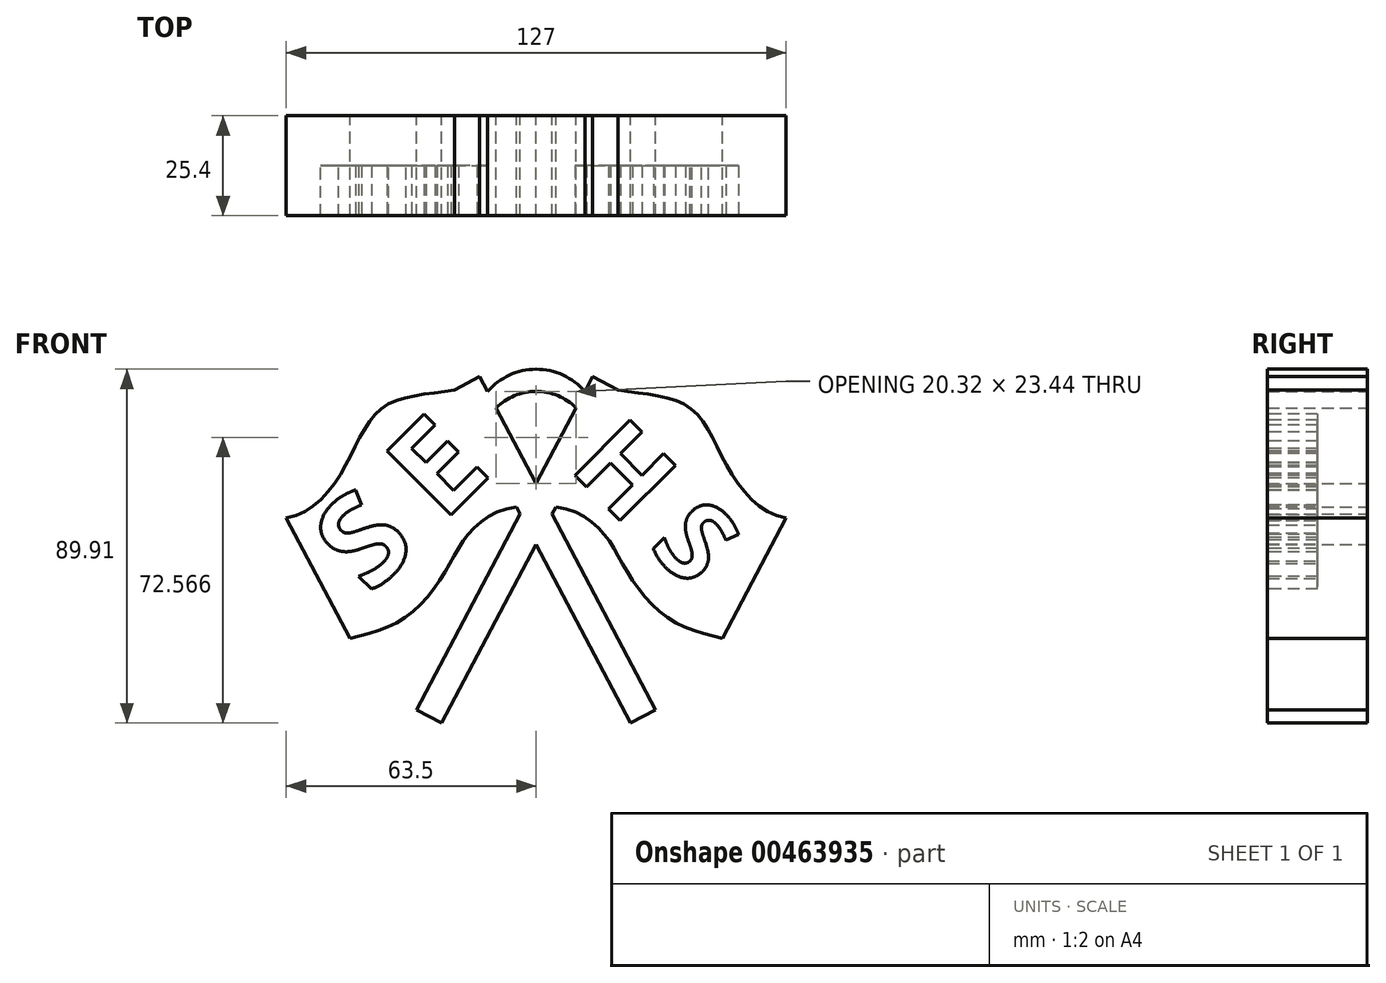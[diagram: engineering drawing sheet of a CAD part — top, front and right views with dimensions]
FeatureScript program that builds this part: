
annotation { "Feature Type Name" : "Feature", "Feature Type Description" : "" }
export const myFeature = defineFeature(function(context is Context, id is Id, definition is map)
    precondition{}
    {
        {
            var Q0;
            Q0=qCreatedBy(makeId("Front.planeOp"),FACE);
            var sketch = newSketch(context, id + "F0", { "sketchPlane" : qUnion([Q0])});
            skFitSpline(sketch, "E0", {"points": [v(20.74, 46.13) * mm, v(38.68, 41.85) * mm, v(48.5, 26.84) * mm, v(63.5, 13.57) * mm], "startDerivative": vector(58.41, -10.52) * mm, "endDerivative": vector(58.76, -8.59) * mm});
            skFitSpline(sketch, "E1.MirrorCS", {"points": [v(-20.74, 46.13) * mm, v(-38.68, 41.85) * mm, v(-48.5, 26.84) * mm, v(-63.5, 13.57) * mm], "startDerivative": vector(-58.41, -10.52) * mm, "endDerivative": vector(-58.76, -8.59) * mm});
            skLineSegment(sketch, "E2", {"start": v(-20.74, 46.13) * mm, "end": v(23.99, -38.53) * mm});
            skLineSegment(sketch, "E3.MirrorCS", {"start": v(20.74, 46.13) * mm, "end": v(-23.99, -38.53) * mm});
            skLineSegment(sketch, "E4", {"start": v(-63.5, 13.57) * mm, "end": v(-47.34, -17.03) * mm});
            skLineSegment(sketch, "E5.MirrorCS", {"start": v(63.5, 13.57) * mm, "end": v(47.34, -17.03) * mm});
            skFitSpline(sketch, "E6", {"points": [v(-47.34, -17.03) * mm, v(-33.48, -11.83) * mm, v(-23.1, 0) * mm, v(-16.74, 10.1) * mm, v(-5, 16.35) * mm], "startDerivative": vector(56.45, 14.98) * mm, "endDerivative": vector(61.73, 6.36) * mm});
            skFitSpline(sketch, "E7.MirrorCS", {"points": [v(47.34, -17.03) * mm, v(33.48, -11.83) * mm, v(23.1, 0) * mm, v(16.74, 10.1) * mm, v(5, 16.35) * mm], "startDerivative": vector(-56.45, 14.98) * mm, "endDerivative": vector(-61.73, 6.36) * mm});
            skLineSegment(sketch, "E8", {"start": v(-20.74, 46.13) * mm, "end": v(-14.36, 49.5) * mm});
            skLineSegment(sketch, "E9", {"start": v(-14.36, 49.5) * mm, "end": v(30.36, -35.16) * mm});
            skLineSegment(sketch, "E10", {"start": v(30.36, -35.16) * mm, "end": v(23.99, -38.53) * mm});
            skLineSegment(sketch, "E11.MirrorCS", {"start": v(14.36, 49.5) * mm, "end": v(-30.36, -35.16) * mm});
            skLineSegment(sketch, "E12.MirrorCS", {"start": v(20.74, 46.13) * mm, "end": v(14.36, 49.5) * mm});
            skLineSegment(sketch, "E13.MirrorCS", {"start": v(-30.36, -35.16) * mm, "end": v(-23.99, -38.53) * mm});
            skSolve(sketch);
        }
        {
            var Q0;
            Q0 = qSketchRegion(id + "F0", true);
            extrude(context, id + "F1", {"entities" : qUnion([Q0]), "depth" : 25.4 * mm});
        }
        {
            var Q0;
            Q0=qCreatedBy(makeId("Front.planeOp"),FACE);
            var sketch = newSketch(context, id + "F2", { "sketchPlane" : qUnion([Q0])});
            skArc(sketch, "E14", {"start": v(14.4, 42.7) * mm, "mid": v(-0.45, 51.38) * mm, "end": v(-14.8, 41.88) * mm});
            skArc(sketch, "E15", {"start": v(12.4, 38.62) * mm, "mid": v(-0.34, 45.75) * mm, "end": v(-12.74, 38.03) * mm});
            skLineSegment(sketch, "E16", {"start": v(-14.8, 41.88) * mm, "end": v(-12.74, 38.03) * mm});
            skLineSegment(sketch, "E17", {"start": v(14.4, 42.7) * mm, "end": v(12.4, 38.62) * mm});
            skSolve(sketch);
        }
        {
            var Q0;
            Q0 = qSketchRegion(id + "F2", true);
            extrude(context, id + "F3", {"entities" : qUnion([Q0]), "operationType" : NewBodyOperationType.ADD, "depth" : 25.4 * mm});
        }
        {
            var Q0;
            Q0=qCreatedBy(makeId("Front.planeOp"),FACE);
            cPlane(context, id + "F4", {"entities" : qUnion([Q0]), "cplaneType" : CPlaneType.OFFSET, "offset" : 25.4 * mm, "width" : 152.4 * mm, "height" : 152.4 * mm});
        }
        {
            var Q0;
            Q0=qCreatedBy(id+"F4.planeOp",FACE);
            var sketch = newSketch(context, id + "F5", { "sketchPlane" : qUnion([Q0])});
            skText(sketch, "E18", { "text": "S E", "fontName": "OpenSans-Bold.ttf"});
            skText(sketch, "E19", { "text": "H S", "fontName": "OpenSans-Bold.ttf"});
            const initialGuessF5  = {"E18": [-0.04214, -0.00623, 0.7071, 0.7071, 0.02325], "E19": [0.00811, 0.02621, 0.7071, -0.7071, 0.01999]};
            skSetInitialGuess(sketch, initialGuessF5);
            skSolve(sketch);
        }
        {
            var Q0;
            Q0 = qSketchRegion(id + "F5", true);
            extrude(context, id + "F6", {"entities" : qUnion([Q0]), "operationType" : NewBodyOperationType.REMOVE, "oppositeDirection" : true, "depth" : 12.7 * mm});
        }
    });
